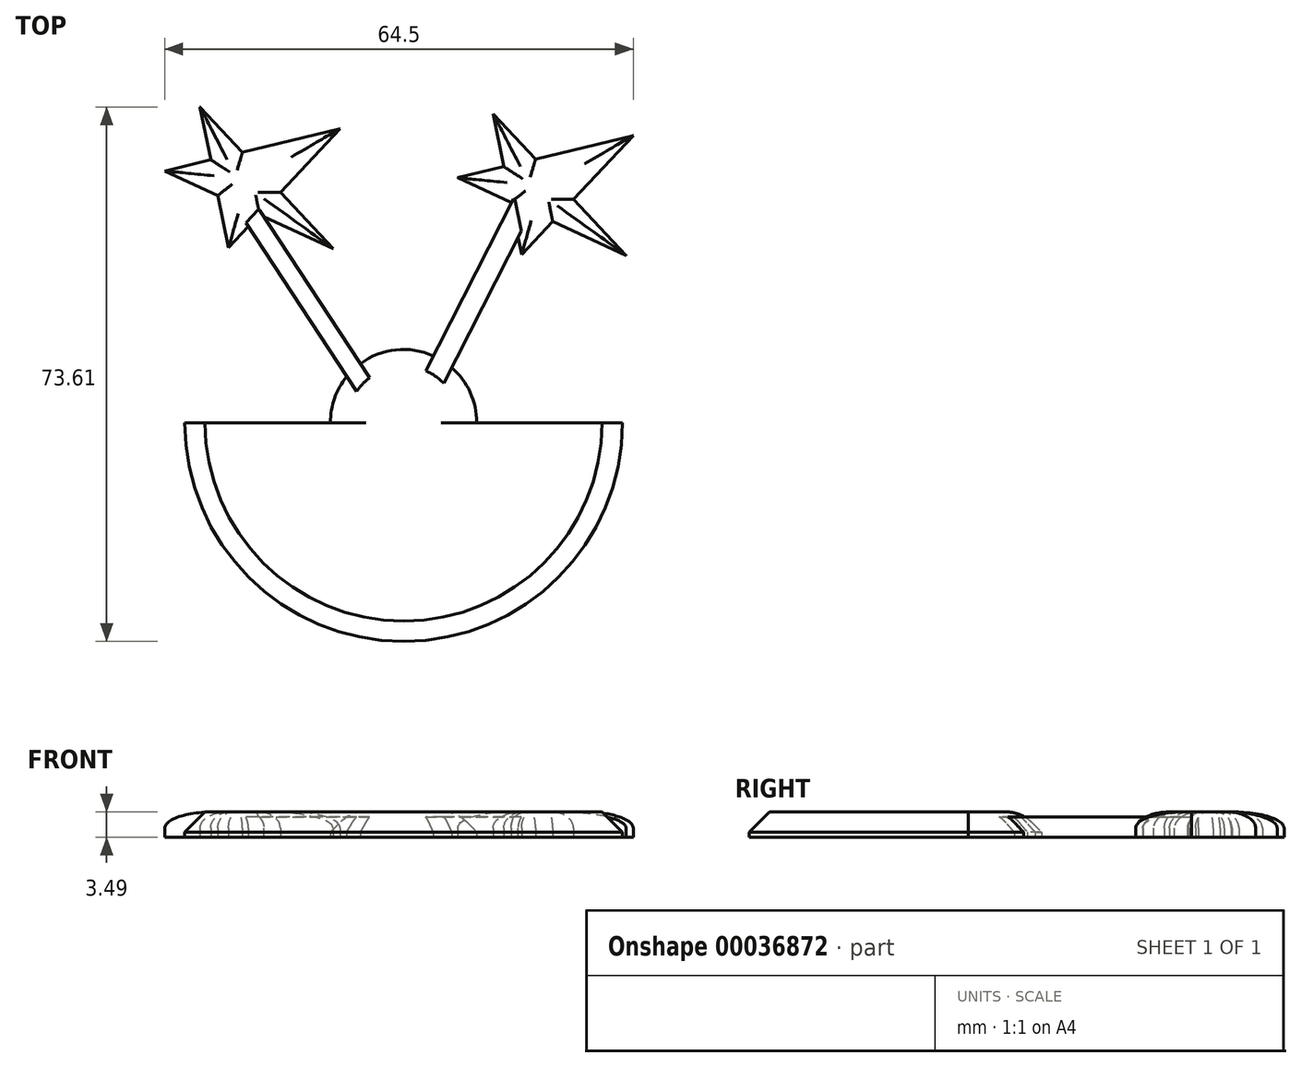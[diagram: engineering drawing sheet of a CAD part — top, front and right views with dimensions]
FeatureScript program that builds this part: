
annotation { "Feature Type Name" : "Feature", "Feature Type Description" : "" }
export const myFeature = defineFeature(function(context is Context, id is Id, definition is map)
    precondition{}
    {
        {
            var Q0;
            Q0=qCreatedBy(makeId("Top.planeOp"),FACE);
            var sketch = newSketch(context, id + "F0", { "sketchPlane" : qUnion([Q0])});
            skArc(sketch, "E0", {"start": v(-27.4, 0) * mm, "mid": v(0, -27.4) * mm, "end": v(27.4, 0) * mm});
            skPoint(sketch, "E1.orphan", {"position": v(-37.94, 0) * mm});
            skLineSegment(sketch, "E2.trimOffspring", {"start": v(-27.4, 0) * mm, "end": v(27.4, 0) * mm});
            skLineSegment(sketch, "E3", {"start": v(0, 0) * mm, "end": v(0, 46.87) * mm, "construction": true});
            skLineSegment(sketch, "E4", {"start": v(-29.9, 31.51) * mm, "end": v(-24.14, 32.9) * mm});
            skLineSegment(sketch, "E5", {"start": v(-7.94, 36.82) * mm, "end": v(-15.42, 28.83) * mm});
            skLineSegment(sketch, "E6", {"start": v(-21.92, 21.89) * mm, "end": v(-23.24, 28.45) * mm});
            skLineSegment(sketch, "E7", {"start": v(-25.48, 39.52) * mm, "end": v(-20.16, 33.87) * mm});
            skLineSegment(sketch, "E8", {"start": v(-8.82, 21.8) * mm, "end": v(-18.03, 26.04) * mm});
            skLineSegment(sketch, "E9.trimOffspring", {"start": v(-20.16, 33.87) * mm, "end": v(-7.94, 36.82) * mm});
            skLineSegment(sketch, "E10.trimOffspring", {"start": v(-24.14, 32.9) * mm, "end": v(-25.48, 39.52) * mm});
            skLineSegment(sketch, "E11.trimOffspring", {"start": v(-23.24, 28.45) * mm, "end": v(-29.9, 31.51) * mm});
            skLineSegment(sketch, "E12.trimOffspring", {"start": v(-18.03, 26.04) * mm, "end": v(-21.92, 21.89) * mm});
            skLineSegment(sketch, "E13.trimOffspring", {"start": v(-15.42, 28.83) * mm, "end": v(-8.82, 21.8) * mm});
            skLineSegment(sketch, "E14.trimOffspring", {"start": v(12.54, 32.05) * mm, "end": v(11.2, 38.67) * mm});
            skLineSegment(sketch, "E15.trimOffspring", {"start": v(18.66, 25.19) * mm, "end": v(14.77, 21.03) * mm});
            skLineSegment(sketch, "E16.trimOffspring", {"start": v(16.52, 33.01) * mm, "end": v(28.74, 35.96) * mm});
            skLineSegment(sketch, "E17.trimOffspring", {"start": v(13.44, 27.59) * mm, "end": v(6.78, 30.66) * mm});
            skLineSegment(sketch, "E18", {"start": v(11.2, 38.67) * mm, "end": v(16.52, 33.01) * mm});
            skLineSegment(sketch, "E19", {"start": v(6.78, 30.66) * mm, "end": v(12.54, 32.05) * mm});
            skLineSegment(sketch, "E20.trimOffspring", {"start": v(21.26, 27.97) * mm, "end": v(27.87, 20.94) * mm});
            skLineSegment(sketch, "E21", {"start": v(28.74, 35.96) * mm, "end": v(21.26, 27.97) * mm});
            skLineSegment(sketch, "E22", {"start": v(14.77, 21.03) * mm, "end": v(13.44, 27.59) * mm});
            skLineSegment(sketch, "E23", {"start": v(27.87, 20.94) * mm, "end": v(18.66, 25.19) * mm});
            skCircle(sketch, "E24", {"center": v(0, 0) * mm, "radius": 9.16 * mm});
            skSolve(sketch);
        }
        {
            var Q0;
            Q0 = qSketchRegion(id + "F0", true);
            extrude(context, id + "F1", {"entities" : qUnion([Q0]), "depth" : 3.17 * mm});
        }
        {
            var Q0;
            Q0=qCreatedBy(makeId("Top.planeOp"),FACE);
            var sketch = newSketch(context, id + "F2", { "sketchPlane" : qUnion([Q0])});
            skLineSegment(sketch, "E25", {"start": v(-19.22, 28.44) * mm, "end": v(-2.06, 2.27) * mm});
            skLineSegment(sketch, "E26", {"start": v(-2.06, 2.27) * mm, "end": v(-4, 1) * mm});
            skLineSegment(sketch, "E27", {"start": v(-4, 1) * mm, "end": v(-21.13, 27.13) * mm});
            skLineSegment(sketch, "E28", {"start": v(-21.13, 27.13) * mm, "end": v(-19.22, 28.44) * mm});
            skLineSegment(sketch, "E29", {"start": v(1.01, 3.04) * mm, "end": v(14.65, 29.76) * mm});
            skLineSegment(sketch, "E30", {"start": v(14.65, 29.76) * mm, "end": v(17.06, 28.53) * mm});
            skLineSegment(sketch, "E31", {"start": v(17.06, 28.53) * mm, "end": v(3.35, 1.66) * mm});
            skLineSegment(sketch, "E32", {"start": v(3.35, 1.66) * mm, "end": v(1.01, 3.04) * mm});
            skSolve(sketch);
        }
        {
            var Q0;
            Q0=makeQuery(id+"F1.opExtrude","CAP_EDGE",EDGE,{"disambiguationData":[OSD([sQuery(id+"F0.wireOp",EDGE,"E0")])],"isStart":false});
            var Q1;
            Q1=makeQuery(id+"F1.opExtrude","CAP_EDGE",EDGE,{"disambiguationData":[OSD([sQuery(id+"F0.wireOp",EDGE,"E24")])],"isStart":false});
            chamfer(context, id + "F3", {"entities" : qUnion([Q0, Q1]), "width" : 2.54 * mm, "tangentPropagation" : true});
        }
        {
            var Q0;
            Q0=makeQuery(id+"F1.opExtrude","CAP_FACE",FACE,{"disambiguationData":[OSD([sQuery(id+"F0.wireOp",EDGE,"E4"),sQuery(id+"F0.wireOp",EDGE,"E5"),sQuery(id+"F0.wireOp",EDGE,"E6"),sQuery(id+"F0.wireOp",EDGE,"E7"),sQuery(id+"F0.wireOp",EDGE,"E8"),sQuery(id+"F0.wireOp",EDGE,"E9.trimOffspring"),sQuery(id+"F0.wireOp",EDGE,"E10.trimOffspring"),sQuery(id+"F0.wireOp",EDGE,"E11.trimOffspring"),sQuery(id+"F0.wireOp",EDGE,"E12.trimOffspring"),sQuery(id+"F0.wireOp",EDGE,"E13.trimOffspring")])],"isStart":false});
            var Q1;
            Q1=makeQuery(id+"F1.opExtrude","CAP_FACE",FACE,{"disambiguationData":[OSD([sQuery(id+"F0.wireOp",EDGE,"E14.trimOffspring"),sQuery(id+"F0.wireOp",EDGE,"E15.trimOffspring"),sQuery(id+"F0.wireOp",EDGE,"E16.trimOffspring"),sQuery(id+"F0.wireOp",EDGE,"E17.trimOffspring"),sQuery(id+"F0.wireOp",EDGE,"E18"),sQuery(id+"F0.wireOp",EDGE,"E19"),sQuery(id+"F0.wireOp",EDGE,"E20.trimOffspring"),sQuery(id+"F0.wireOp",EDGE,"E21"),sQuery(id+"F0.wireOp",EDGE,"E22"),sQuery(id+"F0.wireOp",EDGE,"E23")])],"isStart":false});
            fillet(context, id + "F4", {"entities" : qUnion([Q0, Q1]), "radius" : 2.03 * mm, "tangentPropagation" : true, "allowEdgeOverflow" : false});
        }
        {
            var Q0;
            Q0 = qSketchRegion(id + "F2", true);
            extrude(context, id + "F5", {"entities" : qUnion([Q0]), "operationType" : NewBodyOperationType.ADD, "depth" : 2.54 * mm});
        }
        {
            var Q0;
            Q0=makeQuery(id+"F1.opExtrude","SWEPT_BODY",BODY,{"disambiguationData":[OSD([sQuery(id+"F0.wireOp",EDGE,"E0"),sQuery(id+"F0.wireOp",EDGE,"E2.trimOffspring"),sQuery(id+"F0.wireOp",EDGE,"E24")])]});
            var Q1;
            Q1=qCreatedBy(makeId("Origin.pointOp"),VERTEX);
            transform(context, id + "F6", {"entities" : qUnion([Q0]), "transformType" : TransformType.SCALE_UNIFORMLY, "scale" : 1.1, "makeCopy" : false, "scalePoint" : qUnion([Q1])});
        }
        {
            var Q0;
            {var subQ0=sQuery(id+"F0.wireOp",EDGE,"E24");Q0=makeQuery(id+"F3.opChamfer","BLEND_EDGE",EDGE,{"blendedFrom":[makeQuery(id+"F1.opExtrude","CAP_EDGE",EDGE,{"disambiguationData":[OSD([subQ0])],"isStart":false}),makeQuery(id+"F1.opExtrude","CAP_FACE",FACE,{"disambiguationData":[OSD([sQuery(id+"F0.wireOp",EDGE,"E0"),sQuery(id+"F0.wireOp",EDGE,"E2.trimOffspring"),subQ0])],"isStart":false})],"blendedInto":[makeQuery(id+"F1.opExtrude","CAP_FACE",FACE,{"disambiguationData":[OSD([sQuery(id+"F0.wireOp",EDGE,"E0"),sQuery(id+"F0.wireOp",EDGE,"E2.trimOffspring"),subQ0])],"isStart":false})]});}
            fillet(context, id + "F7", {"entities" : qUnion([Q0]), "radius" : 5.08 * mm, "tangentPropagation" : true, "allowEdgeOverflow" : false});
        }
    });
